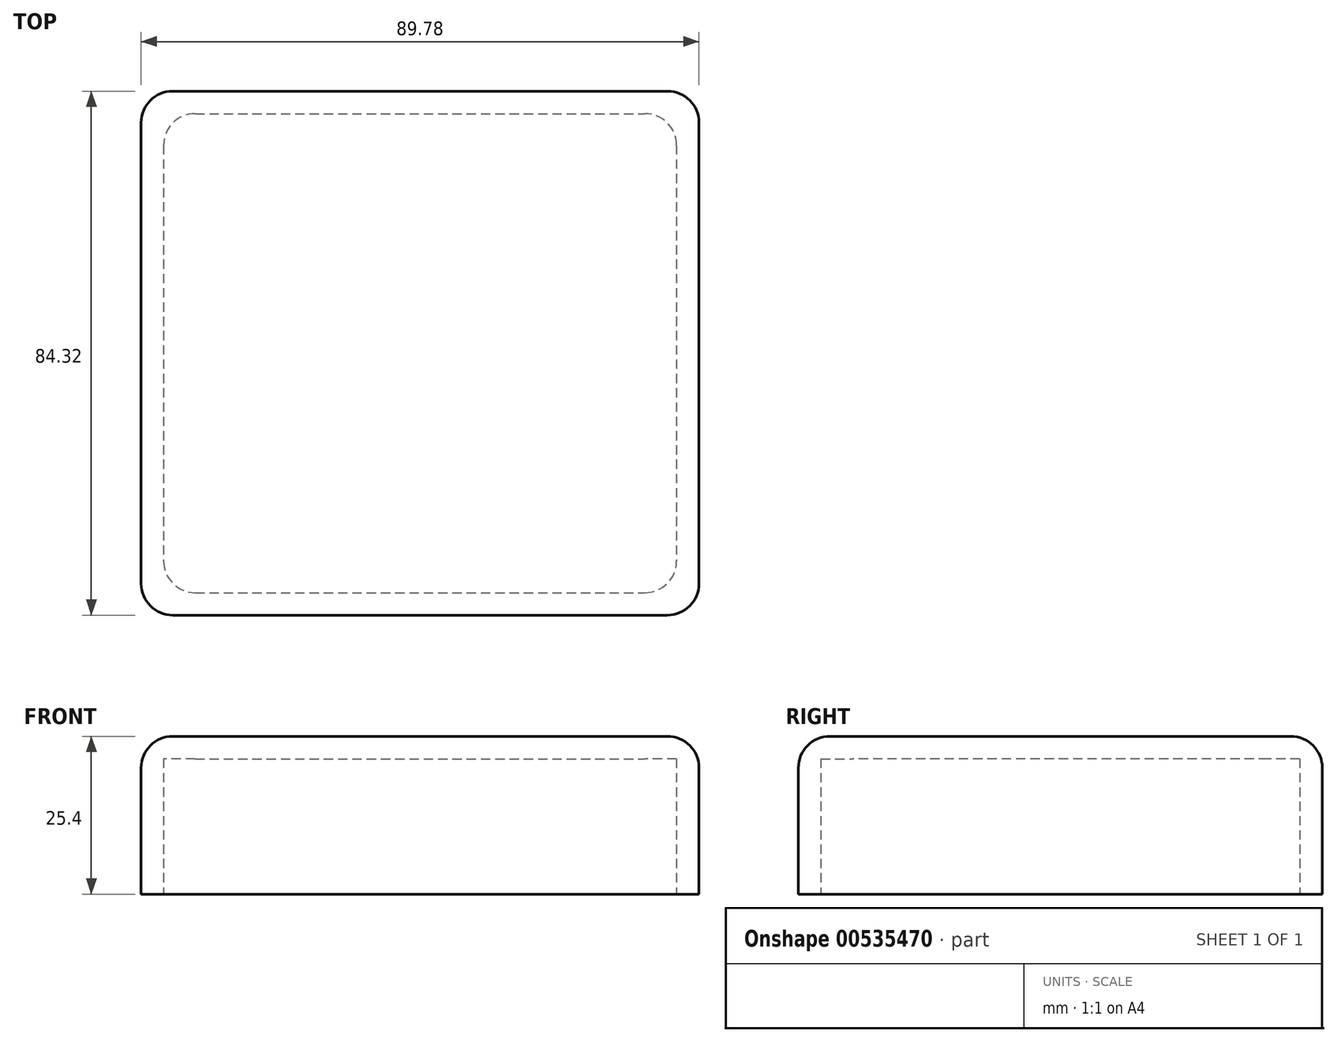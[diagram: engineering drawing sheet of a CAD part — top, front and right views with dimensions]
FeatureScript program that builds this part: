
annotation { "Feature Type Name" : "Feature", "Feature Type Description" : "" }
export const myFeature = defineFeature(function(context is Context, id is Id, definition is map)
    precondition{}
    {
        {
            var Q0;
            Q0=qCreatedBy(makeId("Top.planeOp"),FACE);
            var sketch = newSketch(context, id + "F0", { "sketchPlane" : qUnion([Q0])});
            skLineSegment(sketch, "E0.bottom", {"start": v(-41.28, 38.54) * mm, "end": v(41.28, 38.54) * mm});
            skLineSegment(sketch, "E0.top", {"start": v(-41.27, -38.54) * mm, "end": v(41.28, -38.54) * mm});
            skLineSegment(sketch, "E0.left", {"start": v(-41.28, 38.54) * mm, "end": v(-41.27, -38.54) * mm});
            skLineSegment(sketch, "E0.right", {"start": v(41.27, 38.54) * mm, "end": v(41.28, -38.54) * mm});
            skPoint(sketch, "E0.middle", {"position": v(0, 0) * mm});
            skLineSegment(sketch, "E1", {"start": v(-41.28, 38.54) * mm, "end": v(-44.9, 38.54) * mm});
            skLineSegment(sketch, "E2.bottom", {"start": v(-44.9, 42.16) * mm, "end": v(44.9, 42.16) * mm});
            skLineSegment(sketch, "E2.top", {"start": v(-44.9, -42.16) * mm, "end": v(44.9, -42.16) * mm});
            skLineSegment(sketch, "E2.left", {"start": v(-44.9, 42.16) * mm, "end": v(-44.9, -42.16) * mm});
            skLineSegment(sketch, "E2.right", {"start": v(44.9, 42.16) * mm, "end": v(44.9, -42.16) * mm});
            skSolve(sketch);
        }
        {
            var Q0;
            Q0=makeQuery(id+"F0.imprint","IMPRINT",FACE,{"disambiguationData":[TD([[makeQuery(id+"F0.imprint","IMPRINT",EDGE,{"derivedFrom":sQuery(id+"F0.wireOp",EDGE,"E0.bottom")}),1.0]])]});
            extrude(context, id + "F1", {"entities" : qUnion([Q0]), "depth" : 25.4 * mm, "offsetDistance" : 25.4 * mm});
        }
        {
            var Q0;
            Q0=makeQuery(id+"F1.opExtrude","CAP_FACE",FACE,{"disambiguationData":[OSD([sQuery(id+"F0.wireOp",EDGE,"E0.bottom"),sQuery(id+"F0.wireOp",EDGE,"E0.top"),sQuery(id+"F0.wireOp",EDGE,"E0.left"),sQuery(id+"F0.wireOp",EDGE,"E0.right"),sQuery(id+"F0.wireOp",EDGE,"E2.bottom"),sQuery(id+"F0.wireOp",EDGE,"E2.top"),sQuery(id+"F0.wireOp",EDGE,"E2.left"),sQuery(id+"F0.wireOp",EDGE,"E2.right")])],"isStart":false});
            var sketch = newSketch(context, id + "F2", { "sketchPlane" : qUnion([Q0])});
            skLineSegment(sketch, "E3.bottom", {"start": v(-41.27, -38.54) * mm, "end": v(41.27, -38.54) * mm});
            skLineSegment(sketch, "E3.top", {"start": v(-41.27, 38.54) * mm, "end": v(41.27, 38.54) * mm});
            skLineSegment(sketch, "E3.left", {"start": v(-41.27, -38.54) * mm, "end": v(-41.27, 38.54) * mm});
            skLineSegment(sketch, "E3.right", {"start": v(41.27, -38.54) * mm, "end": v(41.27, 38.54) * mm});
            skPoint(sketch, "E3.middle", {"position": v(0, 0) * mm});
            skSolve(sketch);
        }
        {
            var Q0;
            Q0=makeQuery(id+"F2.imprint","IMPRINT",FACE,{"disambiguationData":[TD([[makeQuery(id+"F2.imprint","IMPRINT",EDGE,{"derivedFrom":sQuery(id+"F2.wireOp",EDGE,"E3.bottom")}),1.0]])]});
            extrude(context, id + "F3", {"entities" : qUnion([Q0]), "operationType" : NewBodyOperationType.ADD, "oppositeDirection" : true, "depth" : 3.62 * mm, "offsetDistance" : 25.4 * mm});
        }
        {
            var Q0;
            Q0=makeQuery(id+"F1.opExtrude","SWEPT_EDGE",EDGE,{"disambiguationData":[OSD([sQuery(id+"F0.wireOp",EDGE,"E0.top"),sQuery(id+"F0.wireOp",EDGE,"E0.right")])]});
            var Q1;
            Q1=makeQuery(id+"F1.opExtrude","SWEPT_EDGE",EDGE,{"disambiguationData":[OSD([sQuery(id+"F0.wireOp",EDGE,"E0.top"),sQuery(id+"F0.wireOp",EDGE,"E0.left")])]});
            var Q2;
            Q2=makeQuery(id+"F1.opExtrude","SWEPT_EDGE",EDGE,{"disambiguationData":[OSD([sQuery(id+"F0.wireOp",EDGE,"E0.bottom"),sQuery(id+"F0.wireOp",EDGE,"E0.right")])]});
            var Q3;
            Q3=makeQuery(id+"F1.opExtrude","SWEPT_EDGE",EDGE,{"disambiguationData":[OSD([sQuery(id+"F0.wireOp",EDGE,"E0.bottom"),sQuery(id+"F0.wireOp",EDGE,"E0.left")])]});
            fillet(context, id + "F4", {"entities" : qUnion([Q0, Q1, Q2, Q3]), "radius" : 5.08 * mm, "tangentPropagation" : true, "allowEdgeOverflow" : false});
        }
        {
            var Q0;
            Q0=makeQuery(id+"F1.opExtrude","SWEPT_EDGE",EDGE,{"disambiguationData":[OSD([sQuery(id+"F0.wireOp",EDGE,"E2.top"),sQuery(id+"F0.wireOp",EDGE,"E2.left")])]});
            var Q1;
            Q1=makeQuery(id+"F1.opExtrude","SWEPT_EDGE",EDGE,{"disambiguationData":[OSD([sQuery(id+"F0.wireOp",EDGE,"E2.top"),sQuery(id+"F0.wireOp",EDGE,"E2.right")])]});
            var Q2;
            Q2=makeQuery(id+"F1.opExtrude","SWEPT_EDGE",EDGE,{"disambiguationData":[OSD([sQuery(id+"F0.wireOp",EDGE,"E2.bottom"),sQuery(id+"F0.wireOp",EDGE,"E2.right")])]});
            var Q3;
            Q3=makeQuery(id+"F1.opExtrude","SWEPT_EDGE",EDGE,{"disambiguationData":[OSD([sQuery(id+"F0.wireOp",EDGE,"E2.bottom"),sQuery(id+"F0.wireOp",EDGE,"E2.left")])]});
            var Q4;
            Q4=makeQuery(id+"F1.opExtrude","CAP_EDGE",EDGE,{"disambiguationData":[OSD([sQuery(id+"F0.wireOp",EDGE,"E2.bottom")])],"isStart":false});
            var Q5;
            Q5=makeQuery(id+"F1.opExtrude","CAP_EDGE",EDGE,{"disambiguationData":[OSD([sQuery(id+"F0.wireOp",EDGE,"E2.left")])],"isStart":false});
            var Q6;
            Q6=makeQuery(id+"F1.opExtrude","CAP_EDGE",EDGE,{"disambiguationData":[OSD([sQuery(id+"F0.wireOp",EDGE,"E2.top")])],"isStart":false});
            var Q7;
            Q7=makeQuery(id+"F1.opExtrude","CAP_EDGE",EDGE,{"disambiguationData":[OSD([sQuery(id+"F0.wireOp",EDGE,"E2.right")])],"isStart":false});
            fillet(context, id + "F5", {"entities" : qUnion([Q0, Q1, Q2, Q3, Q4, Q5, Q6, Q7]), "radius" : 5.08 * mm, "tangentPropagation" : true, "allowEdgeOverflow" : false});
        }
    });
